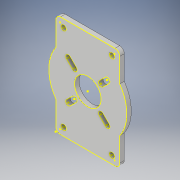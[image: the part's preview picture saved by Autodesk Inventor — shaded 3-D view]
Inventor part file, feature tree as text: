
AUTODESK INVENTOR PART (.ipt)
format: ipt  version: 2019 (Build 230136000, 136)  size: 218,112 bytes
history: native  units: mm
features: sketch x4, extrude x2, hole x1, fillet x1, projected_geometry x1
ambient origin geometry x8: Origin, YZ Plane, XZ Plane, XY Plane, X Axis, Y Axis, Z Axis, Center Point
bodies: Solid1 (feature_tree)
feature tree (9):
  sketch  "Sketch1"  dims[d2=50.0mm d3=17.0mm]
  extrude  "Extrusion1"  Depth=17.0mm
  hole  "Hole1"  [1 undecoded]
  extrude  "Extrusion2"  Depth=25.0mm
  fillet  "Fillet1"  Radius=25.0mm
  sketch  "Sketch4"  dims[d12=25.0mm d13=17.0mm d14=17.0mm d15=8.5mm d16=24.15mm d17=20.15mm d18=32.65mm d20=41.0mm d22=65.3mm d23=5.0mm d25=41.0mm d26=5.0mm d27=16.5mm d28=3.0mm d29=0.0mm d30=17.0mm d31=5.0mm d32=5.0mm d33=5.0mm d34=12.5mm d35=25.0mm d36=25.0mm d37=17.0mm d38=17.0mm d39=8.5mm d40=24.15mm d41=20.15mm d42=32.65mm d43=41.0mm d44=65.3mm d45=5.0mm d46=41.0mm d47=5.0mm d48=16.5mm d49=3.3mm d50=6.0mm d51=4.0mm d52=2.0mm d53=90.0deg d54=8.0mm d55=20.594885mm d56=3.0mm d57=0.0mm d58=3.0mm]
  sketch  "Sketch2"  dims[d4=5.0mm d5=5.0mm d6=5.0mm]
  sketch  "Sketch3"  dims[d7=5.0mm d10=12.5mm d11=25.0mm]
  projected_geometry  "Projected Loop1"
note: 1 required parameter value undecoded (feature->parameter linkage not recoverable at this tier; creation-order binding heuristic only, values carry confidence <= 0.55)
